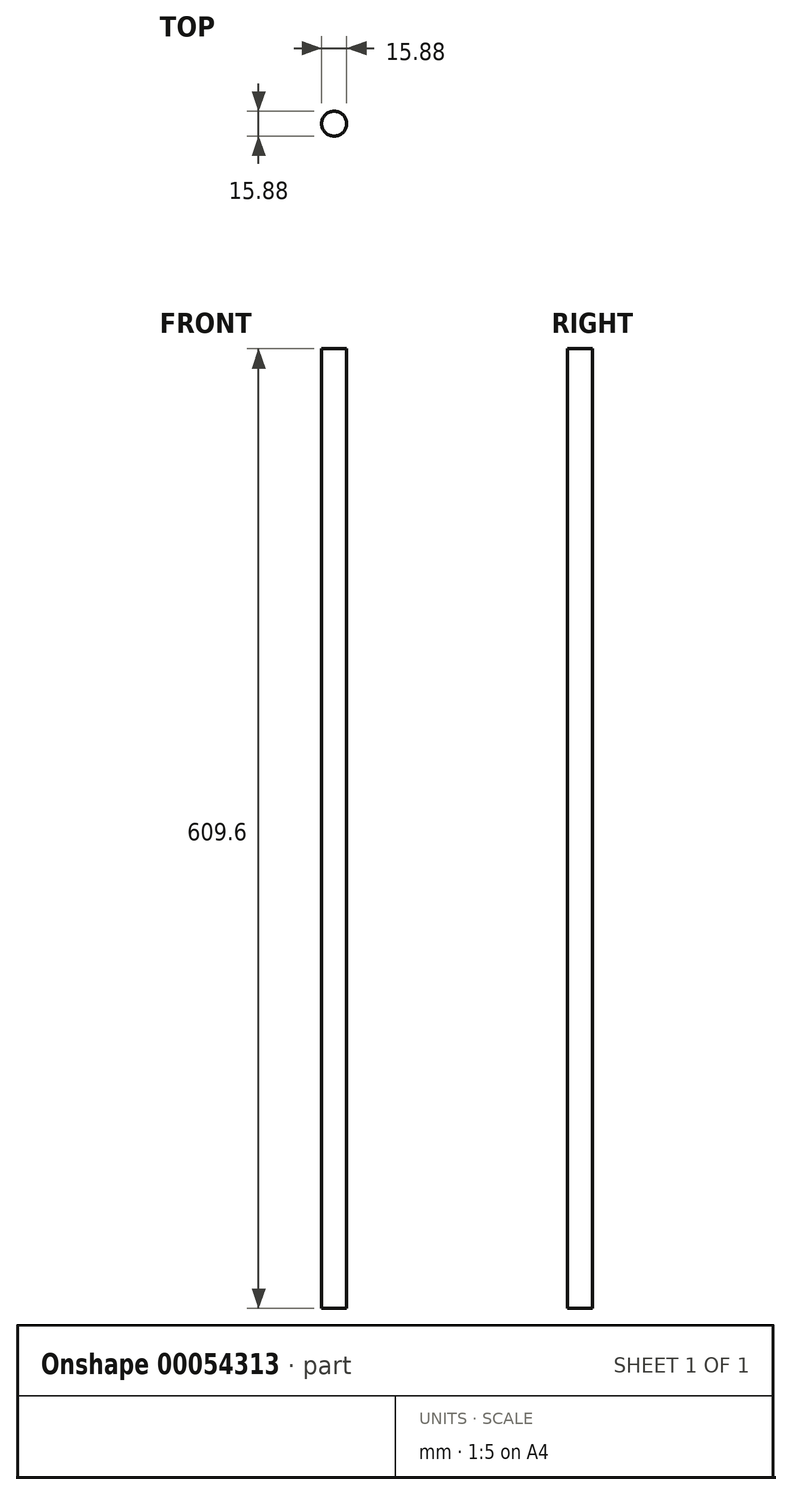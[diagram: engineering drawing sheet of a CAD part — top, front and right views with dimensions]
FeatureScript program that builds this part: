
annotation { "Feature Type Name" : "Feature", "Feature Type Description" : "" }
export const myFeature = defineFeature(function(context is Context, id is Id, definition is map)
    precondition{}
    {
        {
            var Q0;
            Q0=qCreatedBy(makeId("Top.planeOp"),FACE);
            var sketch = newSketch(context, id + "F0", { "sketchPlane" : qUnion([Q0])});
            skCircle(sketch, "E0", {"center": v(0, 0) * mm, "radius": 7.94 * mm});
            skSolve(sketch);
        }
        {
            var Q0;
            Q0=makeQuery(id+"F0.imprint","IMPRINT",FACE,{"disambiguationData":[TD([[makeQuery(id+"F0.imprint","IMPRINT",EDGE,{"derivedFrom":sQuery(id+"F0.wireOp",EDGE,"E0")}),1.0]])]});
            extrude(context, id + "F1", {"entities" : qUnion([Q0]), "depth" : 609.6 * mm});
        }
    });
